# Revit family: Electronics_Monitors_Biamp_Vocia_Passive-End-Of-Line-Devices_PLD___
name_source: partatom
category: Communication Devices
units: mm (PartAtom-declared; Revit-internal decimal feet)

## family parameters
Cut with Voids When Loaded = No
Host = Face
Maintain Annotation Orientation = No
OmniClass Number = 23.85.10.11.11
OmniClass Title = Sound and Signal Devices
Part Type = Normal
Room Calculation Point = No
Round Connector Dimension = Use Diameter
Shared = No

## types (1)
- PLD
    Cable Length = 8.9 "
    Compliance = UL and C-UL listed (USA and Canada), CE Marked (Europe), RoHS Directive (Europe), Evaluated to the requirements of UL 2043 and is suitable for use in air handling spaces
    Default Elevation = 48 "
    Depth = 0.5 "
    Description = Vocia® PLD-1 and PLD-2 Passive End Of Line Devices
    Height = 1.7 "
    Housing Material = Biamp - Plastic - Black
    Line monitoring = 70V/100V constant voltage
    Loudspeaker distance = Up to 4,300ft (1,300m), varies with load and speaker wire gauge
    Manufacturer = Biamp
    Maximum Channel Power Rating = 70V: 150W; 100V: 300W
    Model = Vocia PLD
    Pilot tone = PLD-1: 18.4kHz (VA-8600); PLD-2: 20.2kHz (VA-4300CV, VA-8150CV)
    Product Documentation Link = https://downloads.biamp.com
    Product Page URL = https://www.biamp.com
    Product data url = https://www.bimobject.com
    URL = https://www.biamp.com
    Width = 2.4 "

## geometry (parser evidence)
native form markers: Sweep x2
no freeform markers — native parametric forms only
